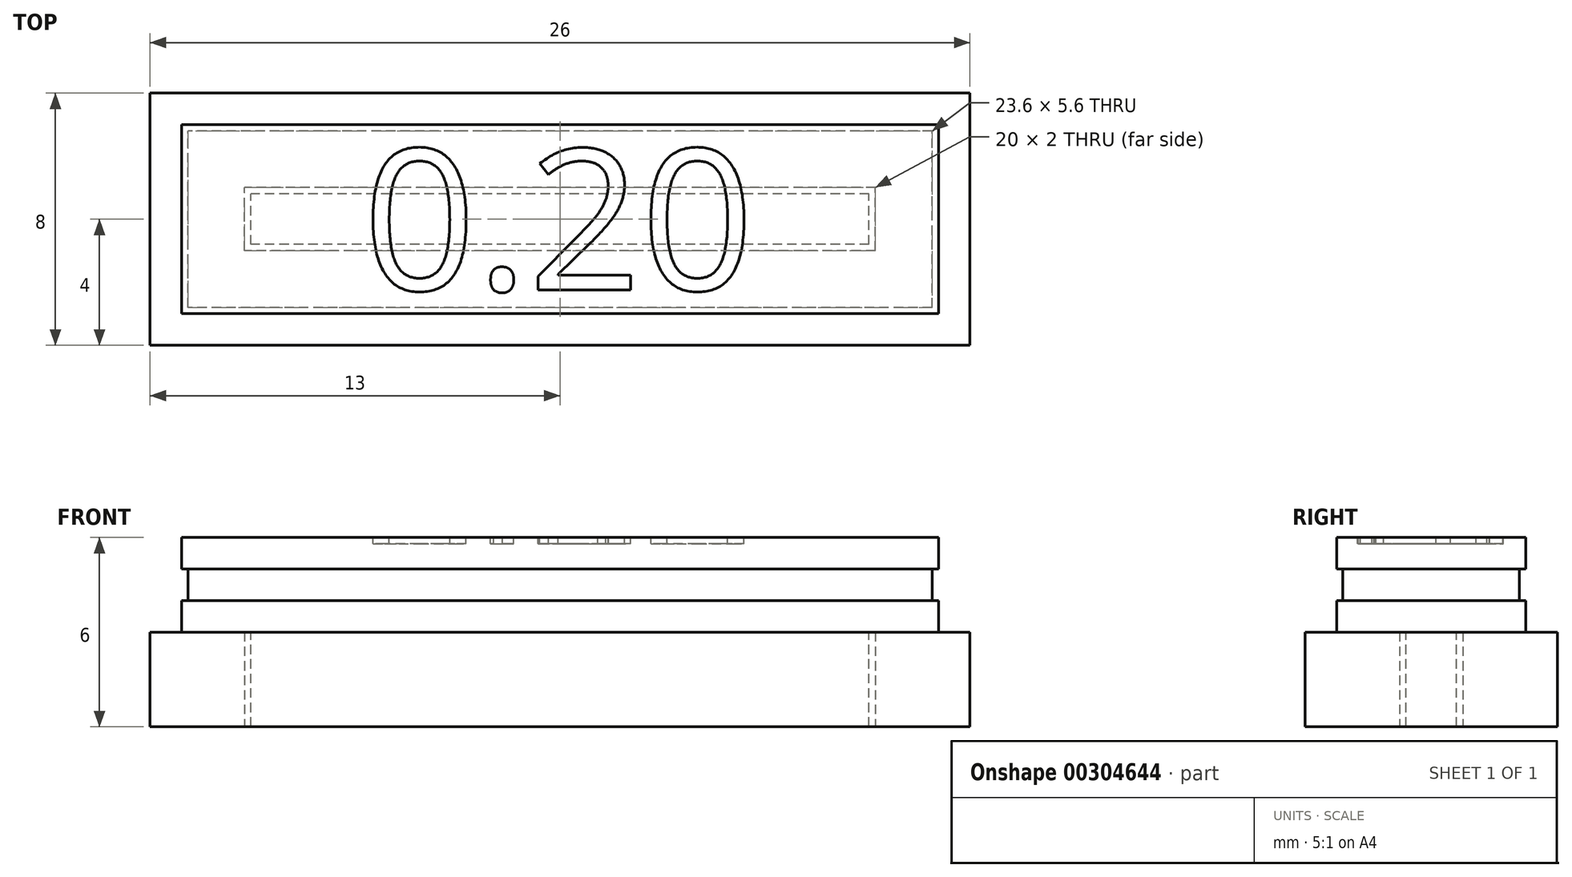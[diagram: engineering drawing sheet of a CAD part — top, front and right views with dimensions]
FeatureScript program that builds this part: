
annotation { "Feature Type Name" : "Feature", "Feature Type Description" : "" }
export const myFeature = defineFeature(function(context is Context, id is Id, definition is map)
    precondition{}
    {
        {
            var Q0;
            Q0=qCreatedBy(makeId("Top.planeOp"),FACE);
            var sketch = newSketch(context, id + "F0", { "sketchPlane" : qUnion([Q0])});
            skLineSegment(sketch, "E0.bottom", {"start": v(10, -1) * mm, "end": v(-10, -1) * mm});
            skLineSegment(sketch, "E0.top", {"start": v(10, 1) * mm, "end": v(-10, 1) * mm});
            skLineSegment(sketch, "E0.left", {"start": v(10, -1) * mm, "end": v(10, 1) * mm});
            skLineSegment(sketch, "E0.right", {"start": v(-10, -1) * mm, "end": v(-10, 1) * mm});
            skPoint(sketch, "E0.middle", {"position": v(0, 0) * mm});
            skLineSegment(sketch, "E1.0", {"start": v(13, 4) * mm, "end": v(-13, 4) * mm});
            skLineSegment(sketch, "E1.1", {"start": v(13, -4) * mm, "end": v(13, 4) * mm});
            skLineSegment(sketch, "E1.2", {"start": v(13, -4) * mm, "end": v(-13, -4) * mm});
            skLineSegment(sketch, "E1.3", {"start": v(-13, -4) * mm, "end": v(-13, 4) * mm});
            skSolve(sketch);
        }
        {
            var Q0;
            Q0 = qSketchRegion(id + "F0", true);
            extrude(context, id + "F1", {"entities" : qUnion([Q0]), "depth" : 3 * mm});
        }
        {
            var Q0;
            Q0=makeQuery(id+"F1.opExtrude","CAP_FACE",FACE,{"disambiguationData":[OSD([sQuery(id+"F0.wireOp",EDGE,"E0.bottom"),sQuery(id+"F0.wireOp",EDGE,"E0.top"),sQuery(id+"F0.wireOp",EDGE,"E0.left"),sQuery(id+"F0.wireOp",EDGE,"E0.right"),sQuery(id+"F0.wireOp",EDGE,"E1.0"),sQuery(id+"F0.wireOp",EDGE,"E1.1"),sQuery(id+"F0.wireOp",EDGE,"E1.2"),sQuery(id+"F0.wireOp",EDGE,"E1.3")])],"isStart":false});
            var sketch = newSketch(context, id + "F2", { "sketchPlane" : qUnion([Q0])});
            skLineSegment(sketch, "E2.0", {"start": v(12, 3) * mm, "end": v(-12, 3) * mm});
            skLineSegment(sketch, "E2.1", {"start": v(12, -3) * mm, "end": v(12, 3) * mm});
            skLineSegment(sketch, "E2.2", {"start": v(12, -3) * mm, "end": v(-12, -3) * mm});
            skLineSegment(sketch, "E2.3", {"start": v(-12, -3) * mm, "end": v(-12, 3) * mm});
            skSolve(sketch);
        }
        {
            var Q0;
            Q0 = qSketchRegion(id + "F2", true);
            extrude(context, id + "F3", {"entities" : qUnion([Q0]), "depth" : 3 * mm});
        }
        {
            var Q0;
            {var subQ0=sQuery(id+"F2.wireOp",EDGE,"E2.0");var subQ1=sQuery(id+"F2.wireOp",EDGE,"E2.3");var subQ2=sQuery(id+"F2.wireOp",EDGE,"E2.1");var subQ3=sQuery(id+"F2.wireOp",EDGE,"E2.2");Q0=makeQuery(id+"F10.boolean.opBoolean","SPLIT",FACE,{"disambiguationData":[TD([makeQuery(id+"F3.opExtrude","SWEPT_FACE",FACE,{"disambiguationData":[OSD([subQ0])]})])],"derivedFrom":makeQuery(id+"F3.opExtrude","CAP_FACE",FACE,{"disambiguationData":[OSD([subQ0,subQ2,subQ3,subQ1])],"isStart":false})});}
            var Q1;
            Q1=makeQuery(id+"F1.opExtrude","CAP_FACE",FACE,{"disambiguationData":[OSD([sQuery(id+"F0.wireOp",EDGE,"E0.bottom"),sQuery(id+"F0.wireOp",EDGE,"E0.top"),sQuery(id+"F0.wireOp",EDGE,"E0.left"),sQuery(id+"F0.wireOp",EDGE,"E0.right"),sQuery(id+"F0.wireOp",EDGE,"E1.0"),sQuery(id+"F0.wireOp",EDGE,"E1.1"),sQuery(id+"F0.wireOp",EDGE,"E1.2"),sQuery(id+"F0.wireOp",EDGE,"E1.3")])],"isStart":false});
            cPlane(context, id + "F4", {"entities" : qUnion([Q0, Q1]), "cplaneType" : CPlaneType.MID_PLANE, "offset" : 25 * mm, "width" : 150 * mm, "height" : 150 * mm});
        }
        {
            var Q0;
            Q0=qCreatedBy(id+"F4.planeOp",FACE);
            var sketch = newSketch(context, id + "F5", { "sketchPlane" : qUnion([Q0])});
            skLineSegment(sketch, "E3.0", {"start": v(12, 3) * mm, "end": v(-12, 3) * mm});
            skLineSegment(sketch, "E3.1", {"start": v(-12, -3) * mm, "end": v(-12, 3) * mm});
            skLineSegment(sketch, "E3.2", {"start": v(12, -3) * mm, "end": v(-12, -3) * mm});
            skLineSegment(sketch, "E3.3", {"start": v(12, -3) * mm, "end": v(12, 3) * mm});
            skLineSegment(sketch, "E4.0", {"start": v(11.8, 2.8) * mm, "end": v(-11.8, 2.8) * mm});
            skLineSegment(sketch, "E4.1", {"start": v(11.8, -2.8) * mm, "end": v(11.8, 2.8) * mm});
            skLineSegment(sketch, "E4.2", {"start": v(11.8, -2.8) * mm, "end": v(-11.8, -2.8) * mm});
            skLineSegment(sketch, "E4.3", {"start": v(-11.8, -2.8) * mm, "end": v(-11.8, 2.8) * mm});
            skSolve(sketch);
        }
        {
            var Q0;
            Q0 = qSketchRegion(id + "F5", true);
            extrude(context, id + "F6", {"entities" : qUnion([Q0]), "operationType" : NewBodyOperationType.REMOVE, "endBound" : BoundingType.SYMMETRIC, "oppositeDirection" : true, "depth" : 1 * mm});
        }
        {
            var Q0;
            Q0=makeQuery(id+"F3.opExtrude","CAP_FACE",FACE,{"disambiguationData":[OSD([sQuery(id+"F2.wireOp",EDGE,"E2.0"),sQuery(id+"F2.wireOp",EDGE,"E2.1"),sQuery(id+"F2.wireOp",EDGE,"E2.2"),sQuery(id+"F2.wireOp",EDGE,"E2.3")])],"isStart":true});
            var sketch = newSketch(context, id + "F7", { "sketchPlane" : qUnion([Q0])});
            skLineSegment(sketch, "E5.0", {"start": v(-9.8, 0.8) * mm, "end": v(-9.8, -0.8) * mm});
            skLineSegment(sketch, "E5.1", {"start": v(9.8, 0.8) * mm, "end": v(-9.8, 0.8) * mm});
            skLineSegment(sketch, "E5.2", {"start": v(9.8, 0.8) * mm, "end": v(9.8, -0.8) * mm});
            skLineSegment(sketch, "E5.3", {"start": v(9.8, -0.8) * mm, "end": v(-9.8, -0.8) * mm});
            skSolve(sketch);
        }
        {
            var Q0;
            Q0 = qSketchRegion(id + "F7", true);
            var Q1;
            Q1=makeQuery(id+"F1.opExtrude","CAP_FACE",FACE,{"disambiguationData":[OSD([sQuery(id+"F0.wireOp",EDGE,"E0.bottom"),sQuery(id+"F0.wireOp",EDGE,"E0.top"),sQuery(id+"F0.wireOp",EDGE,"E0.left"),sQuery(id+"F0.wireOp",EDGE,"E0.right"),sQuery(id+"F0.wireOp",EDGE,"E1.0"),sQuery(id+"F0.wireOp",EDGE,"E1.1"),sQuery(id+"F0.wireOp",EDGE,"E1.2"),sQuery(id+"F0.wireOp",EDGE,"E1.3")])],"isStart":true});
            extrude(context, id + "F8", {"entities" : qUnion([Q0]), "operationType" : NewBodyOperationType.ADD, "endBound" : BoundingType.UP_TO_SURFACE, "endBoundEntityFace" : qUnion([Q1]), "depth" : 25 * mm});
        }
        {
            var Q0;
            Q0=makeQuery(id+"F3.opExtrude","CAP_FACE",FACE,{"disambiguationData":[OSD([sQuery(id+"F2.wireOp",EDGE,"E2.0"),sQuery(id+"F2.wireOp",EDGE,"E2.1"),sQuery(id+"F2.wireOp",EDGE,"E2.2"),sQuery(id+"F2.wireOp",EDGE,"E2.3")])],"isStart":false});
            var sketch = newSketch(context, id + "F9", { "sketchPlane" : qUnion([Q0])});
            skText(sketch, "E6", { "text": "0.20", "fontName": "OpenSans-Regular.ttf"});
            const initialGuessF9  = {"E6": [-0.00624, -0.00225, 1, 0, 0.0045]};
            skSetInitialGuess(sketch, initialGuessF9);
            skSolve(sketch);
        }
        {
            var Q0;
            Q0 = qSketchRegion(id + "F9", true);
            extrude(context, id + "F10", {"entities" : qUnion([Q0]), "operationType" : NewBodyOperationType.REMOVE, "oppositeDirection" : true, "depth" : 0.2 * mm});
        }
    });
